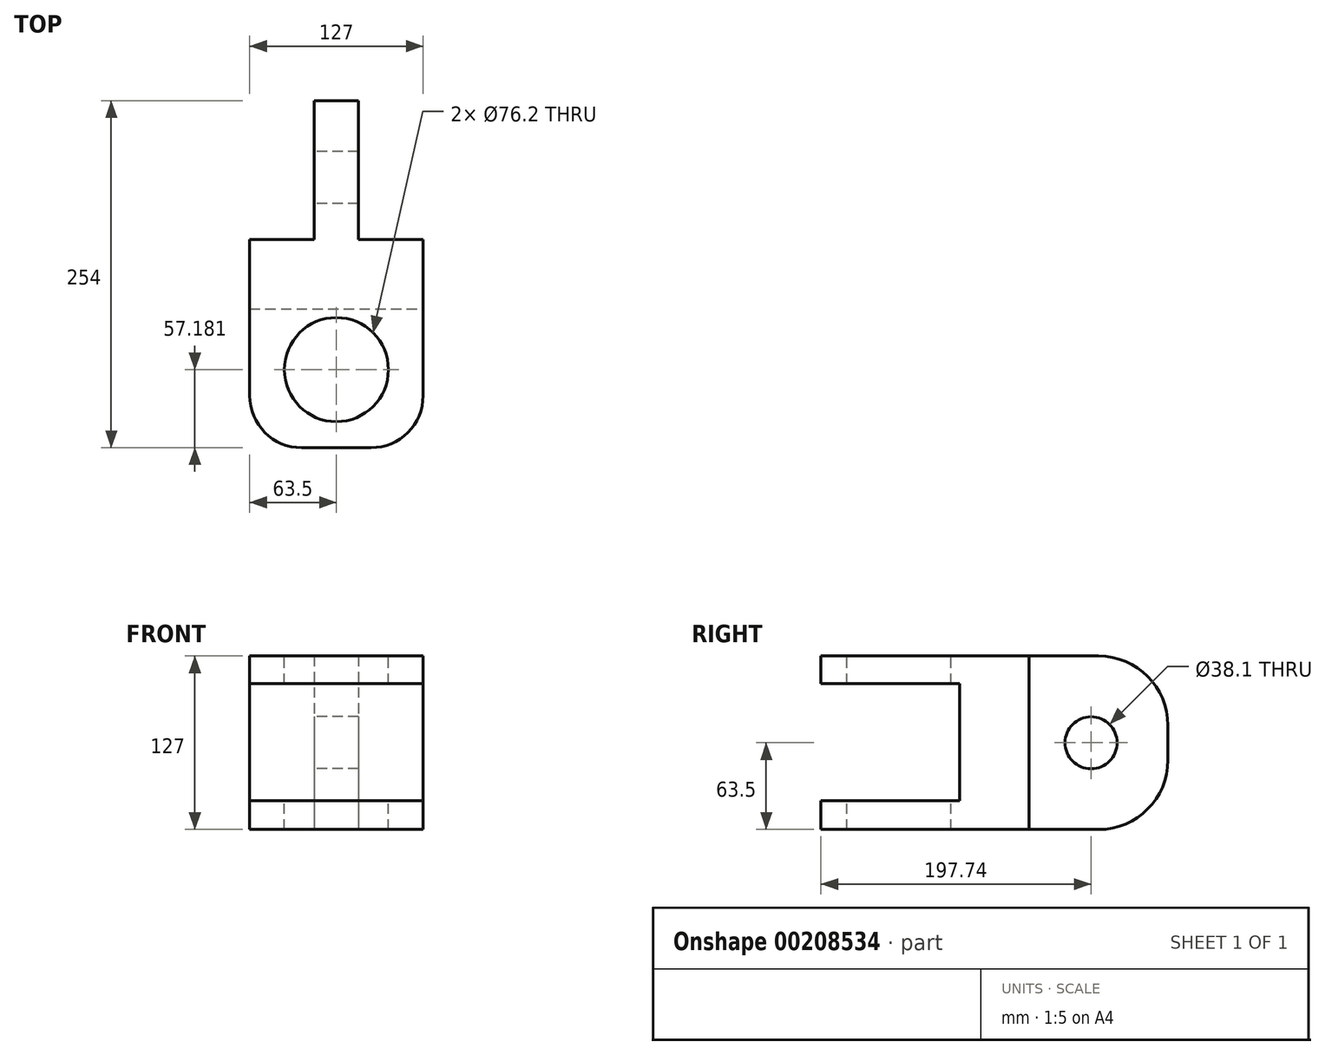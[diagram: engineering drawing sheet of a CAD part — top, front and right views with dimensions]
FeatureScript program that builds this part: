
annotation { "Feature Type Name" : "Feature", "Feature Type Description" : "" }
export const myFeature = defineFeature(function(context is Context, id is Id, definition is map)
    precondition{}
    {
        {
            var Q0;
            Q0=qCreatedBy(makeId("Front.planeOp"),FACE);
            var sketch = newSketch(context, id + "F0", { "sketchPlane" : qUnion([Q0])});
            skLineSegment(sketch, "E0.bottom", {"start": v(-63.5, 63.5) * mm, "end": v(63.5, 63.5) * mm});
            skLineSegment(sketch, "E0.top", {"start": v(-63.5, -63.5) * mm, "end": v(63.5, -63.5) * mm});
            skLineSegment(sketch, "E0.left", {"start": v(-63.5, 63.5) * mm, "end": v(-63.5, -63.5) * mm});
            skLineSegment(sketch, "E0.right", {"start": v(63.5, 63.5) * mm, "end": v(63.5, -63.5) * mm});
            skPoint(sketch, "E0.middle", {"position": v(0, 0) * mm});
            skSolve(sketch);
        }
        {
            var Q0;
            Q0=makeQuery(id+"F0.imprint","IMPRINT",FACE,{"disambiguationData":[TD([[makeQuery(id+"F0.imprint","IMPRINT",EDGE,{"derivedFrom":sQuery(id+"F0.wireOp",EDGE,"E0.bottom")}),-1.0]])]});
            extrude(context, id + "F1", {"entities" : qUnion([Q0]), "depth" : 50.8 * mm});
        }
        {
            var Q0;
            Q0=makeQuery(id+"F1.opExtrude","CAP_FACE",FACE,{"disambiguationData":[OSD([sQuery(id+"F0.wireOp",EDGE,"E0.bottom"),sQuery(id+"F0.wireOp",EDGE,"E0.top"),sQuery(id+"F0.wireOp",EDGE,"E0.left"),sQuery(id+"F0.wireOp",EDGE,"E0.right")])],"isStart":false});
            var sketch = newSketch(context, id + "F2", { "sketchPlane" : qUnion([Q0])});
            skLineSegment(sketch, "E1.bottom", {"start": v(-63.5, 63.5) * mm, "end": v(63.5, 63.5) * mm});
            skLineSegment(sketch, "E1.top", {"start": v(-63.5, 43.21) * mm, "end": v(63.5, 43.21) * mm});
            skLineSegment(sketch, "E1.left", {"start": v(-63.5, 63.5) * mm, "end": v(-63.5, 43.21) * mm});
            skLineSegment(sketch, "E1.right", {"start": v(63.5, 63.5) * mm, "end": v(63.5, 43.21) * mm});
            skLineSegment(sketch, "E2.bottom", {"start": v(-63.5, -63.5) * mm, "end": v(63.5, -63.5) * mm});
            skLineSegment(sketch, "E2.top", {"start": v(-63.5, -42.36) * mm, "end": v(63.5, -42.36) * mm});
            skLineSegment(sketch, "E2.left", {"start": v(-63.5, -63.5) * mm, "end": v(-63.5, -42.36) * mm});
            skLineSegment(sketch, "E2.right", {"start": v(63.5, -63.5) * mm, "end": v(63.5, -42.36) * mm});
            skSolve(sketch);
        }
        {
            var Q0;
            Q0=makeQuery(id+"F2.imprint","IMPRINT",FACE,{"disambiguationData":[TD([[makeQuery(id+"F2.imprint","IMPRINT",EDGE,{"derivedFrom":sQuery(id+"F2.wireOp",EDGE,"E1.bottom")}),-1.0]])]});
            var Q1;
            Q1=makeQuery(id+"F2.imprint","IMPRINT",FACE,{"disambiguationData":[TD([[makeQuery(id+"F2.imprint","IMPRINT",EDGE,{"derivedFrom":sQuery(id+"F2.wireOp",EDGE,"E2.bottom")}),1.0]])]});
            extrude(context, id + "F3", {"entities" : qUnion([Q0, Q1]), "operationType" : NewBodyOperationType.ADD, "depth" : 101.6 * mm});
        }
        {
            var Q0;
            Q0=makeQuery(id+"F3.boolean.opBoolean","MERGE",FACE,{"derivedFrom":[makeQuery(id+"F1.opExtrude","SWEPT_FACE",FACE,{"disambiguationData":[OSD([sQuery(id+"F0.wireOp",EDGE,"E0.bottom")])]}),makeQuery(id+"F3.opExtrude","SWEPT_FACE",FACE,{"disambiguationData":[OSD([sQuery(id+"F2.wireOp",EDGE,"E1.bottom")])]})]});
            var sketch = newSketch(context, id + "F4", { "sketchPlane" : qUnion([Q0])});
            skPoint(sketch, "E3", {"position": v(0, -95.22) * mm});
            skSolve(sketch);
        }
        {
            var Q0;
            Q0=sQuery(id+"F4.wireOp",VERTEX,"E3");
            var Q1;
            Q1=makeQuery(id+"F1.opExtrude","SWEPT_BODY",BODY,{"disambiguationData":[OSD([sQuery(id+"F0.wireOp",EDGE,"E0.bottom"),sQuery(id+"F0.wireOp",EDGE,"E0.top"),sQuery(id+"F0.wireOp",EDGE,"E0.left"),sQuery(id+"F0.wireOp",EDGE,"E0.right")])]});
            hole(context, id + "F5", {"style" : HoleStyle.SIMPLE, "endStyle" : HoleEndStyle.THROUGH, "holeDiameter" : 76.2 * mm, "locations" : qUnion([Q0]), "scope" : qUnion([Q1]), "isTappedThrough" : true});
        }
        {
            var Q0;
            Q0=makeQuery(id+"F3.opExtrude","CAP_EDGE",EDGE,{"disambiguationData":[OSD([sQuery(id+"F2.wireOp",EDGE,"E1.right")])],"isStart":false});
            var Q1;
            Q1=makeQuery(id+"F3.opExtrude","CAP_EDGE",EDGE,{"disambiguationData":[OSD([sQuery(id+"F2.wireOp",EDGE,"E1.left")])],"isStart":false});
            var Q2;
            Q2=makeQuery(id+"F3.opExtrude","CAP_EDGE",EDGE,{"disambiguationData":[OSD([sQuery(id+"F2.wireOp",EDGE,"E2.right")])],"isStart":false});
            var Q3;
            Q3=makeQuery(id+"F3.opExtrude","CAP_EDGE",EDGE,{"disambiguationData":[OSD([sQuery(id+"F2.wireOp",EDGE,"E2.left")])],"isStart":false});
            fillet(context, id + "F6", {"entities" : qUnion([Q0, Q1, Q2, Q3]), "radius" : 38.1 * mm, "tangentPropagation" : true, "allowEdgeOverflow" : false});
        }
        {
            var Q0;
            Q0=makeQuery(id+"F1.opExtrude","CAP_FACE",FACE,{"disambiguationData":[OSD([sQuery(id+"F0.wireOp",EDGE,"E0.bottom"),sQuery(id+"F0.wireOp",EDGE,"E0.top"),sQuery(id+"F0.wireOp",EDGE,"E0.left"),sQuery(id+"F0.wireOp",EDGE,"E0.right")])],"isStart":true});
            var sketch = newSketch(context, id + "F7", { "sketchPlane" : qUnion([Q0])});
            skLineSegment(sketch, "E4.bottom", {"start": v(16.18, 63.5) * mm, "end": v(-16.18, 63.5) * mm});
            skLineSegment(sketch, "E4.top", {"start": v(16.18, -63.5) * mm, "end": v(-16.18, -63.5) * mm});
            skLineSegment(sketch, "E4.left", {"start": v(16.18, 63.5) * mm, "end": v(16.18, -63.5) * mm});
            skLineSegment(sketch, "E4.right", {"start": v(-16.18, 63.5) * mm, "end": v(-16.18, -63.5) * mm});
            skPoint(sketch, "E4.middle", {"position": v(0, 0) * mm});
            skSolve(sketch);
        }
        {
            var Q0;
            Q0=makeQuery(id+"F7.imprint","IMPRINT",FACE,{"disambiguationData":[TD([[makeQuery(id+"F7.imprint","IMPRINT",EDGE,{"derivedFrom":sQuery(id+"F7.wireOp",EDGE,"E4.bottom")}),1.0]])]});
            extrude(context, id + "F8", {"entities" : qUnion([Q0]), "operationType" : NewBodyOperationType.ADD, "depth" : 101.6 * mm});
        }
        {
            var Q0;
            Q0=makeQuery(id+"F8.opExtrude","SWEPT_FACE",FACE,{"disambiguationData":[OSD([sQuery(id+"F7.wireOp",EDGE,"E4.left")])]});
            var sketch = newSketch(context, id + "F9", { "sketchPlane" : qUnion([Q0])});
            skPoint(sketch, "E5", {"position": v(-45.34, 0) * mm});
            skSolve(sketch);
        }
        {
            var Q0;
            Q0=sQuery(id+"F9.wireOp",VERTEX,"E5");
            var Q1;
            Q1=makeQuery(id+"F1.opExtrude","SWEPT_BODY",BODY,{"disambiguationData":[OSD([sQuery(id+"F0.wireOp",EDGE,"E0.bottom"),sQuery(id+"F0.wireOp",EDGE,"E0.top"),sQuery(id+"F0.wireOp",EDGE,"E0.left"),sQuery(id+"F0.wireOp",EDGE,"E0.right")])]});
            hole(context, id + "F10", {"style" : HoleStyle.SIMPLE, "endStyle" : HoleEndStyle.THROUGH, "holeDiameter" : 38.1 * mm, "locations" : qUnion([Q0]), "scope" : qUnion([Q1]), "isTappedThrough" : true});
        }
        {
            var Q0;
            Q0=makeQuery(id+"F8.opExtrude","CAP_EDGE",EDGE,{"disambiguationData":[OSD([sQuery(id+"F7.wireOp",EDGE,"E4.bottom")])],"isStart":false});
            var Q1;
            Q1=makeQuery(id+"F8.opExtrude","CAP_EDGE",EDGE,{"disambiguationData":[OSD([sQuery(id+"F7.wireOp",EDGE,"E4.top")])],"isStart":false});
            fillet(context, id + "F11", {"entities" : qUnion([Q0, Q1]), "radius" : 50.8 * mm, "tangentPropagation" : true, "allowEdgeOverflow" : false});
        }
    });
